# Revit family: Ontologia Pendant
name_source: partatom
category: Lighting Fixtures
units: mm (PartAtom-declared; Revit-internal decimal feet)

## family parameters
Cut with Voids When Loaded = No
Host = Face
Light Source = Yes
Part Type = Normal
Room Calculation Point = No
Round Connector Dimension = Use Diameter
Shared = No

## types (1)
- Ontologia Pendant
    Apparent Load = 0 VA
    Color Filter = 16777215
    Cord Thickness = 0' - 0 1/4"
    Cord Type = HM - Sable Cord
    Default Elevation = 3' - 8"
    Description = Hand molded glass pendant
    Diffuser = HM - Diffuser
    Dimming Lamp Color Temperature Shift = <None>
    Emit Shape Visible in Rendering = No
    Emit from Circle Diameter = 0' - 7"
    Glass Color = HM - Rose Glass
    Lamp = LED
    Manufacturer = HennepinMade
    Metal Finishing = HM - OxBlood PC
    Model = Ontologia Pendant
    Photometric Web File = 2ACLX4_30L.ies
    Tilt Angle = -90.00°
    Type Comments = Ontologia
    URL = https://hennepinmade.com
    Wattage Comments = 3
    Wood Finish = HM - Mahogany

## geometry (parser evidence)
native form markers: Sweep x2
no freeform markers — native parametric forms only
